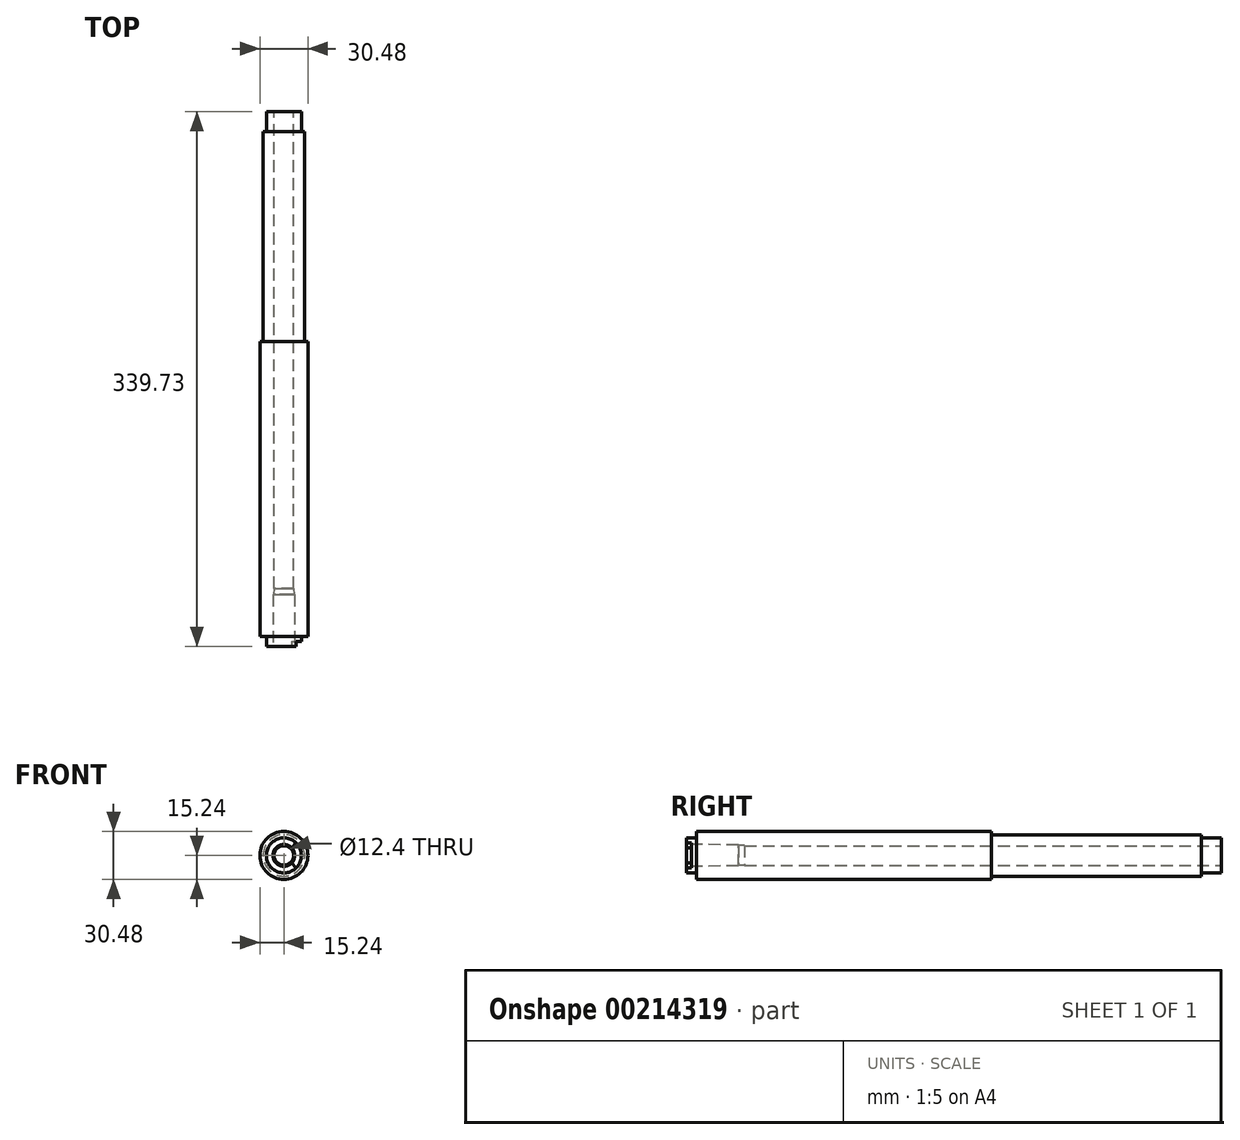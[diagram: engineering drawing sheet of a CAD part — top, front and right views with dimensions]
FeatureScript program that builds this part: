
annotation { "Feature Type Name" : "Feature", "Feature Type Description" : "" }
export const myFeature = defineFeature(function(context is Context, id is Id, definition is map)
    precondition{}
    {
        {
            var Q0;
            Q0=qCreatedBy(makeId("Right.planeOp"),FACE);
            var sketch = newSketch(context, id + "F0", { "sketchPlane" : qUnion([Q0])});
            skLineSegment(sketch, "E0", {"start": v(0, 0) * mm, "end": v(0, 11.11) * mm});
            skLineSegment(sketch, "E1", {"start": v(6.35, 15.24) * mm, "end": v(193.68, 15.24) * mm});
            skLineSegment(sketch, "E2", {"start": v(339.73, 11.11) * mm, "end": v(339.73, 0) * mm});
            skLineSegment(sketch, "E3", {"start": v(339.73, 0) * mm, "end": v(0, 0) * mm});
            skLineSegment(sketch, "E4", {"start": v(406.4, 6.2) * mm, "end": v(36.86, 6.2) * mm});
            skLineSegment(sketch, "E5", {"start": v(36.86, 6.2) * mm, "end": v(32.94, 6.39) * mm});
            skLineSegment(sketch, "E6", {"start": v(32.94, 6.39) * mm, "end": v(32.94, 6.74) * mm});
            skLineSegment(sketch, "E7", {"start": v(32.94, 6.74) * mm, "end": v(0, 6.94) * mm});
            skLineSegment(sketch, "E8", {"start": v(339.73, 11.11) * mm, "end": v(327.03, 11.11) * mm});
            skLineSegment(sketch, "E9", {"start": v(327.03, 11.11) * mm, "end": v(327.03, 13.18) * mm});
            skLineSegment(sketch, "E10", {"start": v(327.03, 13.18) * mm, "end": v(193.68, 13.18) * mm});
            skLineSegment(sketch, "E11", {"start": v(193.68, 13.18) * mm, "end": v(193.68, 15.24) * mm});
            skPoint(sketch, "E12.orphan", {"position": v(327.03, 15.24) * mm});
            skLineSegment(sketch, "E13", {"start": v(0, 11.11) * mm, "end": v(6.35, 11.11) * mm});
            skLineSegment(sketch, "E14", {"start": v(6.35, 11.11) * mm, "end": v(6.35, 15.24) * mm});
            skSolve(sketch);
        }
        {
            var Q0;
            {var subQ2=sQuery(id+"F0.wireOp",EDGE,"E1");Q0=makeQuery(id+"F0.imprint","IMPRINT",FACE,{"disambiguationData":[TD([[makeQuery(id+"F0.imprint","IMPRINT",EDGE,{"derivedFrom":subQ2}),-1.0]])]});}
            var Q1;
            Q1=sQuery(id+"F0.wireOp",EDGE,"E3");
            revolve(context, id + "F1", {"entities" : qUnion([Q0]), "axis" : qUnion([Q1]), "revolveType" : RevolveType.FULL});
        }
        {
            var Q0;
            Q0=qCreatedBy(makeId("Top.planeOp"),FACE);
            var sketch = newSketch(context, id + "F2", { "sketchPlane" : qUnion([Q0])});
            skCircle(sketch, "E15", {"center": v(0, 355.6) * mm, "radius": 1.59 * mm});
            skSolve(sketch);
        }
        {
            var Q0;
            Q0 = qSketchRegion(id + "F2", true);
            extrude(context, id + "F3", {"entities" : qUnion([Q0]), "operationType" : NewBodyOperationType.REMOVE, "depth" : 25.4 * mm});
        }
        {
            var Q0;
            Q0=makeQuery(id+"F1.opRevolve","SWEPT_FACE",FACE,{"disambiguationData":[OSD([sQuery(id+"F0.wireOp",EDGE,"E0")])]});
            var sketch = newSketch(context, id + "F4", { "sketchPlane" : qUnion([Q0])});
            skLineSegment(sketch, "E16", {"start": v(0, 0) * mm, "end": v(9.2, 9.2) * mm});
            skLineSegment(sketch, "E17", {"start": v(0, 0) * mm, "end": v(14.16, -14.16) * mm});
            skLineSegment(sketch, "E18", {"start": v(14.16, -14.16) * mm, "end": v(23.1, -14.16) * mm});
            skLineSegment(sketch, "E19", {"start": v(23.1, -14.16) * mm, "end": v(23.1, 9.65) * mm});
            skLineSegment(sketch, "E20", {"start": v(23.1, 9.65) * mm, "end": v(9.2, 9.2) * mm});
            skSolve(sketch);
        }
        {
            var Q0;
            Q0 = qSketchRegion(id + "F4", true);
            extrude(context, id + "F5", {"entities" : qUnion([Q0]), "operationType" : NewBodyOperationType.REMOVE, "oppositeDirection" : true, "depth" : 3.17 * mm});
        }
    });
